# Revit family: TY-FRB-TY4831_Metric
name_source: partatom
category: Sprinklers
revit_build: Autodesk Revit 2016 (Build: 20150220_1215(x64)
units: mm (PartAtom-declared; Revit-internal decimal feet)

## family parameters
Always vertical = Yes
Cut with Voids When Loaded = No
Maintain Annotation Orientation = No
OmniClass Number = 23.65.70.17.11.24
OmniClass Title = Fire Fighting Sprinkler Heads
Part Type = Normal
Room Calculation Point = No
Round Connector Dimension = Use Diameter
Shared = No
Work Plane-Based = No

## types (22) — shared parameters
COBie = Yes
COBie.Component.Name = Sprinklers:Upright_SIN
COBie.Type = Yes
COBie.Type.AssetType = Fixed
COBie.Type.Category = Pr_70_55_97_84:Sprinklers
COBie.Type.DurationUnit = year
COBie.Type.Manufacturer = Tyco Fire Protection Products
COBie.Type.Material = Bronze
COBie.Type.Shape = Cylinder
COBie.Type.WarrantyGuarantorParts = http://tycofsbp.com
Coverage = Standard
Coverage_ = Standard
K-Factor = 114.87
Manufacturer = Tyco Fire Protection Products
Manufacturer URL = www.tyco-fire.com
Material_ = Bronze
Model = TY-FRB
Nominal Diameter 1 = 15 mm
Orifice = Extra Large
Orifice Size = 13 mm
Outside Diameter 1 = 21 mm
Response = Quick
Response_ = Quick
SIN No = TY4831
Takeout 1 = 56 mm
Technical Data Sheet No = TFP171
zero-valued in all types: COBie.Type.NominalHeight, COBie.Type.NominalLength, COBie.Type.NominalWidth, COBie.Type.ReplacementCost, Style Id

## per-type parameters (varying)
| type | COBie.Component.Description | COBie.Type.Colour | COBie.Type.Finish | COBie.Type.ModelNumber | COBie.Type.ModelReference | COBie.Type.Size | Description | Finish_ | Part No | Temperature Rating |
| Wet Upright_135  57.2°C K115 DN15 NPT Br_57-360-1-135 | TY-FRB Wet Upright  57.2°C K115 DN15 NPT Br | Yellow | Natural Brass | 57-360-1-135 | TY-FRB Wet Upright  57.2°C K115 DN15 NPT Br | 1/2"(DN15) | TY-FRB Wet Upright_135  57.2°C K115 DN15 NPT Br | Natural Brass | 57-360-1-135 | 135 °C |
| Wet Upright_155  68.3°C K115 DN15 NPT Br_57-360-1-155 | TY-FRB Wet Upright  68.3°C K115 DN15 NPT Br | Yellow | Natural Brass | 57-360-1-155 | TY-FRB Wet Upright  68.3°C K115 DN15 NPT Br | 1/2"(DN15) | TY-FRB Wet Upright_155  68.3°C K115 DN15 NPT Br | Natural Brass | 57-360-1-155 | 155 °C |
| Wet Upright_175  79.4°C K115 DN15 NPT Br_57-360-1-175 | TY-FRB Wet Upright  79.4°C K115 DN15 NPT Br | Yellow | natural Brass | 57-360-1-175 | TY-FRB Wet Upright  79.4°C K115 DN15 NPT Br | 1/2"(DN15) | TY-FRB Wet Upright_175  79.4°C K115 DN15 NPT Br | Natural Brass | 57-360-1-175 | 175 °C |
| Wet Upright_200  93.3°C K115 DN15 NPT Br_57-360-1-200 | TY-FRB Wet Upright  93.3°C K115 DN15 NPT Br | Yellow | Natural Brass | 57-360-1-200 | TY-FRB Wet Upright  93.3°C K115 DN15 NPT Br | 1/2"(DN15) | TY-FRB Wet Upright_200  93.3°C K115 DN15 NPT Br | Natural Brass | 57-360-1-200 | 200 °C |
| Wet Upright_286  141.1°C K115 DN15 NPT Br_57-360-1-286 | TY-FRB Wet Upright  141.1°C K115 DN15 NPT Br | Yellow | Natural Brass | 57-360-1-286 | TY-FRB Wet Upright  141.1°C K115 DN15 NPT Br | 1/2"(DN15) | TY-FRB Wet Upright_286  141.1°C K115 DN15 NPT Br | Natural Brass | 57-360-1-286 | 286 °C |
| Wet Upright_135  57.2°C K115 DN15 NPT Wh_57-360-4-135 | TY-FRB Wet Upright  135°F K8.0 1/2 NPT Wh | White | Signal White | 57-360-4-135 | TY-FRB Wet Upright  135°F K8.0 1/2 NPT Wh | 1/2"(DN15) | TY-FRB Wet Upright_135  57.2°C K115 DN15 NPT Wh | White RAL9003 | 57-360-4-135 | 135 °C |
| Wet Upright_155  57.2°C K115 DN15 NPT Wh_57-360-4-155 | TY-FRB Wet Upright_White_135  135°F K8.0 1/2 NPT Wh | White | Signal White | 57-360-4-155 | TY-FRB Wet Upright_White_135  135°F K8.0 1/2 NPT Wh | 1/2"(DN15) | TY-FRB Wet Upright_155  57.2°C K115 DN15 NPT Wh | White RAL9003 | 57-360-4-155 | 155 °C |
| Wet Upright_175  57.2°C K115 DN15 NPT Wh_57-360-4-175 | TY-FRB Wet Upright_White_155  135°F K8.0 1/2 NPT Wh | White | Signal White | 57-360-4-175 | TY-FRB Wet Upright_White_155  135°F K8.0 1/2 NPT Wh | 1/2"(DN15) | TY-FRB Wet Upright_175  57.2°C K115 DN15 NPT Wh | White RAL9003 | 57-360-4-175 | 175 °C |
| Wet Upright_200  57.2°C K115 DN15 NPT Wh_57-360-4-200 | TY-FRB Wet Upright_White_175  135°F K8.0 1/2 NPT Wh | White | Signal White | 57-360-4-200 | TY-FRB Wet Upright_White_175  135°F K8.0 1/2 NPT Wh | 1/2"(DN15) | TY-FRB Wet Upright_200  57.2°C K115 DN15 NPT Wh | White RAL9003 | 57-360-4-200 | 200 °C |
| Wet Upright_286  57.2°C K115 DN15 NPT Wh_57-360-4-286 | TY-FRB Wet Upright_White_200  135°F K8.0 1/2 NPT Wh | White | Signal White | 57-360-4-286 | TY-FRB Wet Upright_White_200  135°F K8.0 1/2 NPT Wh | 1/2"(DN15) | TY-FRB Wet Upright_286  57.2°C K115 DN15 NPT Wh | White RAL9003 | 57-360-4-286 | 286 °C |
| Wet Upright_155  57.2°C K115 DN15 NPT Jet Black_57-360-5-155 | TY-FRB Wet Upright_White_155  135°F K8.0 1/2 NPT Wh | Black | Jet Black | 57-360-5-155 | TY-FRB Wet Upright_White_155  135°F K8.0 1/2 NPT Wh | 1/2"(DN15) | TY-FRB Wet Upright_155  57.2°C K115 DN15 NPT Jet Black | Jet Black RAL9005 | 57-360-5-155 | 155 °C |
| Wet Upright_200  57.2°C K115 DN15 NPT Jet Black_57-360-5-200 | TY-FRB Wet Upright_Black_155   135°F K8.0 1/2 NPT Wh | Black | Jet black | 57-360-5-200 | TY-FRB Wet Upright_Black_155   135°F K8.0 1/2 NPT Wh | 1/2"(DN15) | TY-FRB Wet Upright_200  57.2°C K115 DN15 NPT Jet Black | Jet Black RAL9005 | 57-360-5-200 | 200 °C |
| Wet Upright_135  57.2°C K115 DN15 NPT Lead_57-360-7-135 | TY-FRB Wet Upright  57.2°C K115 DN15 NPT Lead | Gray | Lead Coated | 57-360-7-135 | TY-FRB Wet Upright  57.2°C K115 DN15 NPT Lead | 1/2"(DN15) | TY-FRB Wet Upright_135  57.2°C K115 DN15 NPT Lead | Lead Coated | 57-360-7-135 | 135 °C |
| Wet Upright_155  68.3°C K115 DN15 NPT Lead_57-360-7-155 | TY-FRB Wet Upright  68.3°C K115 DN15 NPT Lead | Gray | Lead Coated | 57-360-7-155 | TY-FRB Wet Upright  68.3°C K115 DN15 NPT Lead | 1/2"(DN15) | TY-FRB Wet Upright_155  68.3°C K115 DN15 NPT Lead | Lead Coated | 57-360-7-155 | 155 °C |
| Wet Upright_175  79.4°C K115 DN15 NPT Lead_57-360-7-175 | TY-FRB Wet Upright  79.4°C K115 DN15 NPT Lead | Gray | Lead Coated | 57-360-7-175 | TY-FRB Wet Upright  79.4°C K115 DN15 NPT Lead | 1/2"(DN15) | TY-FRB Wet Upright_175  79.4°C K115 DN15 NPT Lead | Lead Coated | 57-360-7-175 | 175 °C |
| Wet Upright_200  93.3°C K115 DN15 NPT Lead_57-360-7-200 | TY-FRB Wet Upright  93.3°C K115 DN15 NPT Lead | Gray | Lead Coated | 57-360-7-200 | TY-FRB Wet Upright  93.3°C K115 DN15 NPT Lead | 1/2"(DN15) | TY-FRB Wet Upright_200  93.3°C K115 DN15 NPT Lead | Lead Coated | 57-360-7-200 | 200 °C |
| Wet Upright_286  141.1°C K115 DN15 NPT Lead_57-360-7-286 | TY-FRB Wet Upright  141.1°C K115 DN15 NPT Lead | Gray | Lead Coated | 57-360-7-286 | TY-FRB Wet Upright  141.1°C K115 DN15 NPT Lead | 1/2'(DN15) | TY-FRB Wet Upright_286  141.1°C K115 DN15 NPT Lead | Lead Coated | 57-360-7-286 | 286 °C |
| Wet Upright_135  57.2°C K115 DN15 NPT Chr_57-360-9-135 | TY-FRB Wet Upright  57.2°C K115 DN15 NPT Chr | Silver | Chrome Plated | 57-360-9-135 | TY-FRB Wet Upright  57.2°C K115 DN15 NPT Chr | 1/2"(DN15) | TY-FRB Wet Upright_135  57.2°C K115 DN15 NPT Chr | Chrome Plated | 57-360-9-135 | 135 °C |
| Wet Upright_155  68.3°C K115 DN15 NPT Chr_57-360-9-155 | TY-FRB Wet Upright  68.3°C K115 DN15 NPT Chr | Silver | Chrome Plated | 57-360-9-155 | TY-FRB Wet Upright  68.3°C K115 DN15 NPT Chr | 1/2"(DN15) | TY-FRB Wet Upright_155  68.3°C K115 DN15 NPT Chr | Chrome Plated | 57-360-9-155 | 155 °C |
| Wet Upright_175  79.4°C K115 DN15 NPT Chr_57-360-9-175 | TY-FRB Wet Upright  79.4°C K115 DN15 NPT Chr | Silver | Chrome Plated | 57-360-9-175 | TY-FRB Wet Upright  79.4°C K115 DN15 NPT Chr | 1/2"(DN15) | TY-FRB Wet Upright_175  79.4°C K115 DN15 NPT CHROME | Chrome Plated | 57-360-9-175 | 175 °C |
| Wet Upright_200 57.2°C K115 DN15 NPT Chr_57-360-9-200 | TY-FRB Wet Upright  93.3°C K115 DN15 NPT Chr | Silver | Chrome Plated | 57-360-9-200 | TY-FRB Wet Upright  93.3°C K115 DN15 NPT Chr | 1/2"(DN15) | TY-FRB Wet Upright_200  93.3°C K115 DN15 NPT CHROME | Chrome Plated | 57-360-9-200 | 200 °C |
| Wet Upright_286 141.1°C K115 DN15 NPT Chr_57-360-9-286 | TY-FRB Wet Upright  141.1°C K115 DN15 NPT Chr | Silver | Chrome Plated | 57-360-9-286 | TY-FRB Wet Upright  141.1°C K115 DN15 NPT Chr | 1/2"(DN15) | TY-FRB Wet Upright_286  57.2°C K115 DN15 NPT CHROME | Chrome Plated | 57-360-9-286 | 286 °C |

## geometry (parser evidence)
native form markers: Blend x2, Sweep x66
no freeform markers — native parametric forms only
